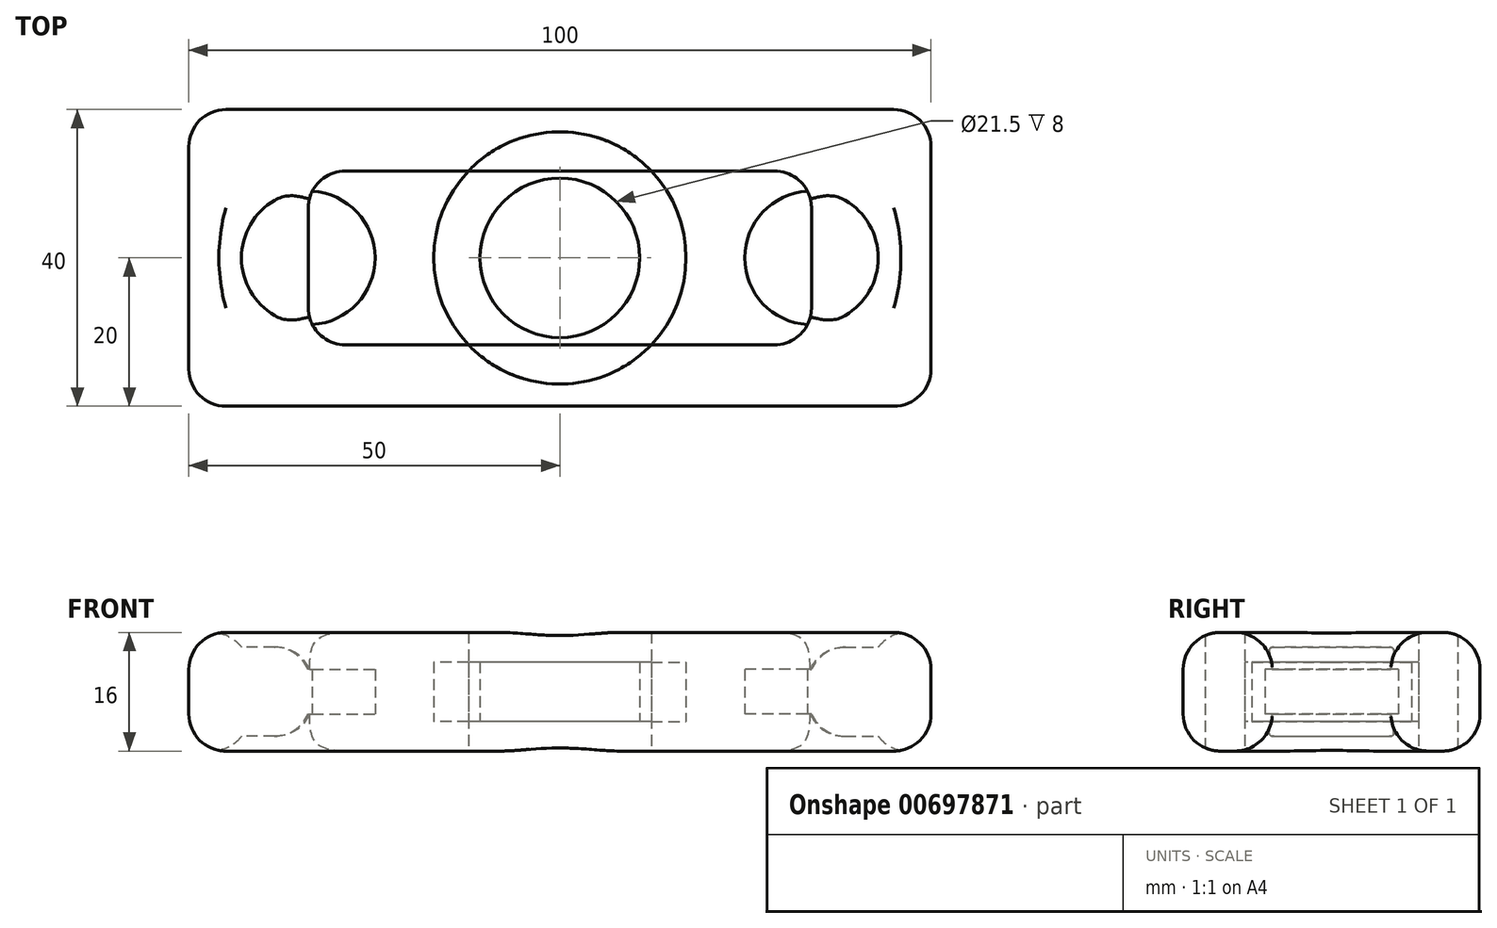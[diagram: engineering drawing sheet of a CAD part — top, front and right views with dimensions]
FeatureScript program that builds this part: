
annotation { "Feature Type Name" : "Feature", "Feature Type Description" : "" }
export const myFeature = defineFeature(function(context is Context, id is Id, definition is map)
    precondition{}
    {
        {
            var Q0;
            Q0=qCreatedBy(makeId("Top.planeOp"),FACE);
            var sketch = newSketch(context, id + "F0", { "sketchPlane" : qUnion([Q0])});
            skLineSegment(sketch, "E0.bottom", {"start": v(45, -20) * mm, "end": v(-45, -20) * mm});
            skLineSegment(sketch, "E0.top", {"start": v(45, 20) * mm, "end": v(-45, 20) * mm});
            skLineSegment(sketch, "E0.left", {"start": v(50, -15) * mm, "end": v(50, 15) * mm});
            skLineSegment(sketch, "E0.right", {"start": v(-50, -15) * mm, "end": v(-50, 15) * mm});
            skPoint(sketch, "E0.middle", {"position": v(0, 0) * mm});
            skCircle(sketch, "E1", {"center": v(0, 0) * mm, "radius": 10.75 * mm});
            skPoint(sketch, "E2.visualSharp", {"position": v(-50, 20) * mm});
            skArc(sketch, "E2.filletArc", {"start": v(-45, 20) * mm, "mid": v(-48.54, 18.54) * mm, "end": v(-50, 15) * mm});
            skPoint(sketch, "E3.visualSharp", {"position": v(-50, -20) * mm});
            skArc(sketch, "E3.filletArc", {"start": v(-50, -15) * mm, "mid": v(-48.54, -18.54) * mm, "end": v(-45, -20) * mm});
            skPoint(sketch, "E4.visualSharp", {"position": v(50, -20) * mm});
            skArc(sketch, "E4.filletArc", {"start": v(45, -20) * mm, "mid": v(48.54, -18.54) * mm, "end": v(50, -15) * mm});
            skPoint(sketch, "E5.visualSharp", {"position": v(50, 20) * mm});
            skArc(sketch, "E5.filletArc", {"start": v(50, 15) * mm, "mid": v(48.54, 18.54) * mm, "end": v(45, 20) * mm});
            skCircle(sketch, "E6", {"center": v(0, 0) * mm, "radius": 17 * mm});
            skLineSegment(sketch, "E7.bottom", {"start": v(28.9, -11.72) * mm, "end": v(-28.9, -11.72) * mm});
            skLineSegment(sketch, "E7.top", {"start": v(28.9, 11.72) * mm, "end": v(-28.9, 11.72) * mm});
            skLineSegment(sketch, "E7.left", {"start": v(33.9, -6.72) * mm, "end": v(33.9, 6.72) * mm});
            skLineSegment(sketch, "E7.right", {"start": v(-33.9, -6.72) * mm, "end": v(-33.9, 6.72) * mm});
            skPoint(sketch, "E8.visualSharp", {"position": v(-33.9, 11.72) * mm});
            skArc(sketch, "E8.filletArc", {"start": v(-28.9, 11.72) * mm, "mid": v(-32.44, 10.25) * mm, "end": v(-33.9, 6.72) * mm});
            skPoint(sketch, "E9.visualSharp", {"position": v(33.9, 11.72) * mm});
            skArc(sketch, "E9.filletArc", {"start": v(33.9, 6.72) * mm, "mid": v(32.44, 10.25) * mm, "end": v(28.9, 11.72) * mm});
            skPoint(sketch, "E10.visualSharp", {"position": v(33.9, -11.72) * mm});
            skArc(sketch, "E10.filletArc", {"start": v(28.9, -11.72) * mm, "mid": v(32.44, -10.25) * mm, "end": v(33.9, -6.72) * mm});
            skPoint(sketch, "E11.visualSharp", {"position": v(-33.9, -11.72) * mm});
            skArc(sketch, "E11.filletArc", {"start": v(-33.9, -6.72) * mm, "mid": v(-32.44, -10.25) * mm, "end": v(-28.9, -11.72) * mm});
            skCircle(sketch, "E12", {"center": v(-33.9, 0) * mm, "radius": 9 * mm});
            skCircle(sketch, "E13", {"center": v(33.9, 0) * mm, "radius": 9 * mm});
            skSolve(sketch);
        }
        {
            var Q0;
            Q0=makeQuery(id+"F0.imprint","IMPRINT",FACE,{"disambiguationData":[TD([[makeQuery(id+"F0.imprint","IMPRINT",EDGE,{"derivedFrom":sQuery(id+"F0.wireOp",EDGE,"E0.bottom")}),-1.0]])]});
            extrude(context, id + "F1", {"entities" : qUnion([Q0]), "endBound" : BoundingType.SYMMETRIC, "depth" : 16 * mm, "offsetDistance" : 25 * mm});
        }
        {
            var Q0;
            {var subQ1=sQuery(id+"F0.wireOp",EDGE,"E7.top");var subQ5=sQuery(id+"F0.wireOp",EDGE,"E6");var subQ6=makeQuery(id+"F0.imprint","INTERSECT",VERTEX,{"disambiguationData":[OD(0.0)],"derivedFrom":[subQ5,subQ1]});Q0=makeQuery(id+"F0.imprint","IMPRINT",FACE,{"disambiguationData":[TD([[makeQuery(id+"F0.imprint","IMPRINT",EDGE,{"disambiguationData":[TD([[subQ6,-1.0]])],"derivedFrom":subQ5}),-1.0]])]});}
            var Q1;
            {var subQ1=sQuery(id+"F0.wireOp",EDGE,"E7.top");var subQ8=sQuery(id+"F0.wireOp",EDGE,"E6");var subQ10=makeQuery(id+"F0.imprint","INTERSECT",VERTEX,{"disambiguationData":[OD(1.0)],"derivedFrom":[subQ8,subQ1]});Q1=makeQuery(id+"F0.imprint","IMPRINT",FACE,{"disambiguationData":[TD([[makeQuery(id+"F0.imprint","IMPRINT",EDGE,{"disambiguationData":[TD([[subQ10,1.0]])],"derivedFrom":subQ8}),-1.0]])]});}
            extrude(context, id + "F2", {"entities" : qUnion([Q0, Q1]), "operationType" : NewBodyOperationType.ADD, "endBound" : BoundingType.SYMMETRIC, "depth" : 10 * mm, "offsetDistance" : 25 * mm});
        }
        {
            var Q0;
            {var subQ0=sQuery(id+"F0.wireOp",EDGE,"E7.right");Q0=makeQuery(id+"F0.imprint","IMPRINT",FACE,{"disambiguationData":[TD([[makeQuery(id+"F0.imprint","IMPRINT",EDGE,{"derivedFrom":subQ0}),1.0]])]});}
            var Q1;
            {var subQ0=sQuery(id+"F0.wireOp",EDGE,"E7.left");Q1=makeQuery(id+"F0.imprint","IMPRINT",FACE,{"disambiguationData":[TD([[makeQuery(id+"F0.imprint","IMPRINT",EDGE,{"derivedFrom":subQ0}),-1.0]])]});}
            extrude(context, id + "F3", {"entities" : qUnion([Q0, Q1]), "operationType" : NewBodyOperationType.ADD, "endBound" : BoundingType.SYMMETRIC, "depth" : 12 * mm, "offsetDistance" : 25 * mm});
        }
        {
            var Q0;
            Q0=makeQuery(id+"F0.imprint","IMPRINT",FACE,{"disambiguationData":[TD([[makeQuery(id+"F0.imprint","IMPRINT",EDGE,{"derivedFrom":sQuery(id+"F0.wireOp",EDGE,"E1")}),-1.0]])]});
            var Q1;
            {var subQ0=sQuery(id+"F0.wireOp",EDGE,"E7.top");var subQ1=sQuery(id+"F0.wireOp",EDGE,"E6");var subQ2=makeQuery(id+"F0.imprint","INTERSECT",VERTEX,{"disambiguationData":[OD(0.0)],"derivedFrom":[subQ1,subQ0]});Q1=makeQuery(id+"F0.imprint","IMPRINT",FACE,{"disambiguationData":[TD([[makeQuery(id+"F0.imprint","IMPRINT",EDGE,{"disambiguationData":[TD([[subQ2,1.0]])],"derivedFrom":subQ1}),1.0]])]});}
            var Q2;
            {var subQ0=sQuery(id+"F0.wireOp",EDGE,"E7.bottom");var subQ1=sQuery(id+"F0.wireOp",EDGE,"E6");var subQ2=makeQuery(id+"F0.imprint","INTERSECT",VERTEX,{"disambiguationData":[OD(0.0)],"derivedFrom":[subQ1,subQ0]});Q2=makeQuery(id+"F0.imprint","IMPRINT",FACE,{"disambiguationData":[TD([[makeQuery(id+"F0.imprint","IMPRINT",EDGE,{"disambiguationData":[TD([[subQ2,-1.0]])],"derivedFrom":subQ1}),1.0]])]});}
            extrude(context, id + "F4", {"entities" : qUnion([Q0, Q1, Q2]), "operationType" : NewBodyOperationType.ADD, "endBound" : BoundingType.SYMMETRIC, "depth" : 8 * mm, "offsetDistance" : 25 * mm});
        }
        {
            var Q0;
            {var subQ0=sQuery(id+"F0.wireOp",EDGE,"E7.right");Q0=makeQuery(id+"F0.imprint","IMPRINT",FACE,{"disambiguationData":[TD([[makeQuery(id+"F0.imprint","IMPRINT",EDGE,{"derivedFrom":subQ0}),-1.0]])]});}
            var Q1;
            {var subQ0=sQuery(id+"F0.wireOp",EDGE,"E7.left");Q1=makeQuery(id+"F0.imprint","IMPRINT",FACE,{"disambiguationData":[TD([[makeQuery(id+"F0.imprint","IMPRINT",EDGE,{"derivedFrom":subQ0}),1.0]])]});}
            extrude(context, id + "F5", {"entities" : qUnion([Q0, Q1]), "operationType" : NewBodyOperationType.ADD, "endBound" : BoundingType.SYMMETRIC, "depth" : 6 * mm, "offsetDistance" : 25 * mm});
        }
        {
            var Q0;
            Q0=makeQuery(id+"F1.opExtrude","CAP_EDGE",EDGE,{"disambiguationData":[OSD([sQuery(id+"F0.wireOp",EDGE,"E0.top")])],"isStart":true});
            fillet(context, id + "F6", {"entities" : qUnion([Q0]), "radius" : 5 * mm, "tangentPropagation" : true, "allowEdgeOverflow" : false});
        }
        {
            var Q0;
            Q0=makeQuery(id+"F1.opExtrude","CAP_EDGE",EDGE,{"disambiguationData":[OSD([sQuery(id+"F0.wireOp",EDGE,"E0.top")])],"isStart":false});
            fillet(context, id + "F7", {"entities" : qUnion([Q0]), "radius" : 5 * mm, "tangentPropagation" : true, "allowEdgeOverflow" : false});
        }
        {
            var Q0;
            Q0=makeQuery(id+"F1.opExtrude","CAP_EDGE",EDGE,{"disambiguationData":[OSD([sQuery(id+"F0.wireOp",EDGE,"E12")])],"isStart":true});
            var Q1;
            Q1=makeQuery(id+"F1.opExtrude","CAP_EDGE",EDGE,{"disambiguationData":[OSD([sQuery(id+"F0.wireOp",EDGE,"E13")])],"isStart":true});
            var Q2;
            Q2=makeQuery(id+"F1.opExtrude","CAP_EDGE",EDGE,{"disambiguationData":[OSD([sQuery(id+"F0.wireOp",EDGE,"E12")])],"isStart":false});
            var Q3;
            Q3=makeQuery(id+"F1.opExtrude","CAP_EDGE",EDGE,{"disambiguationData":[OSD([sQuery(id+"F0.wireOp",EDGE,"E13")])],"isStart":false});
            fillet(context, id + "F8", {"entities" : qUnion([Q0, Q1, Q2, Q3]), "radius" : 5 * mm, "tangentPropagation" : true, "allowEdgeOverflow" : false});
        }
        {
            var Q0;
            Q0=makeQuery(id+"F3.opExtrude","CAP_EDGE",EDGE,{"disambiguationData":[OSD([sQuery(id+"F0.wireOp",EDGE,"E7.left")])],"isStart":false});
            var Q1;
            Q1=makeQuery(id+"F3.opExtrude","CAP_EDGE",EDGE,{"disambiguationData":[OSD([sQuery(id+"F0.wireOp",EDGE,"E7.right")])],"isStart":false});
            var Q2;
            Q2=makeQuery(id+"F3.opExtrude","CAP_EDGE",EDGE,{"disambiguationData":[OSD([sQuery(id+"F0.wireOp",EDGE,"E7.right")])],"isStart":true});
            var Q3;
            Q3=makeQuery(id+"F3.opExtrude","CAP_EDGE",EDGE,{"disambiguationData":[OSD([sQuery(id+"F0.wireOp",EDGE,"E7.left")])],"isStart":true});
            fillet(context, id + "F9", {"entities" : qUnion([Q0, Q1, Q2, Q3]), "radius" : 5 * mm, "tangentPropagation" : true, "allowEdgeOverflow" : false});
        }
    });
